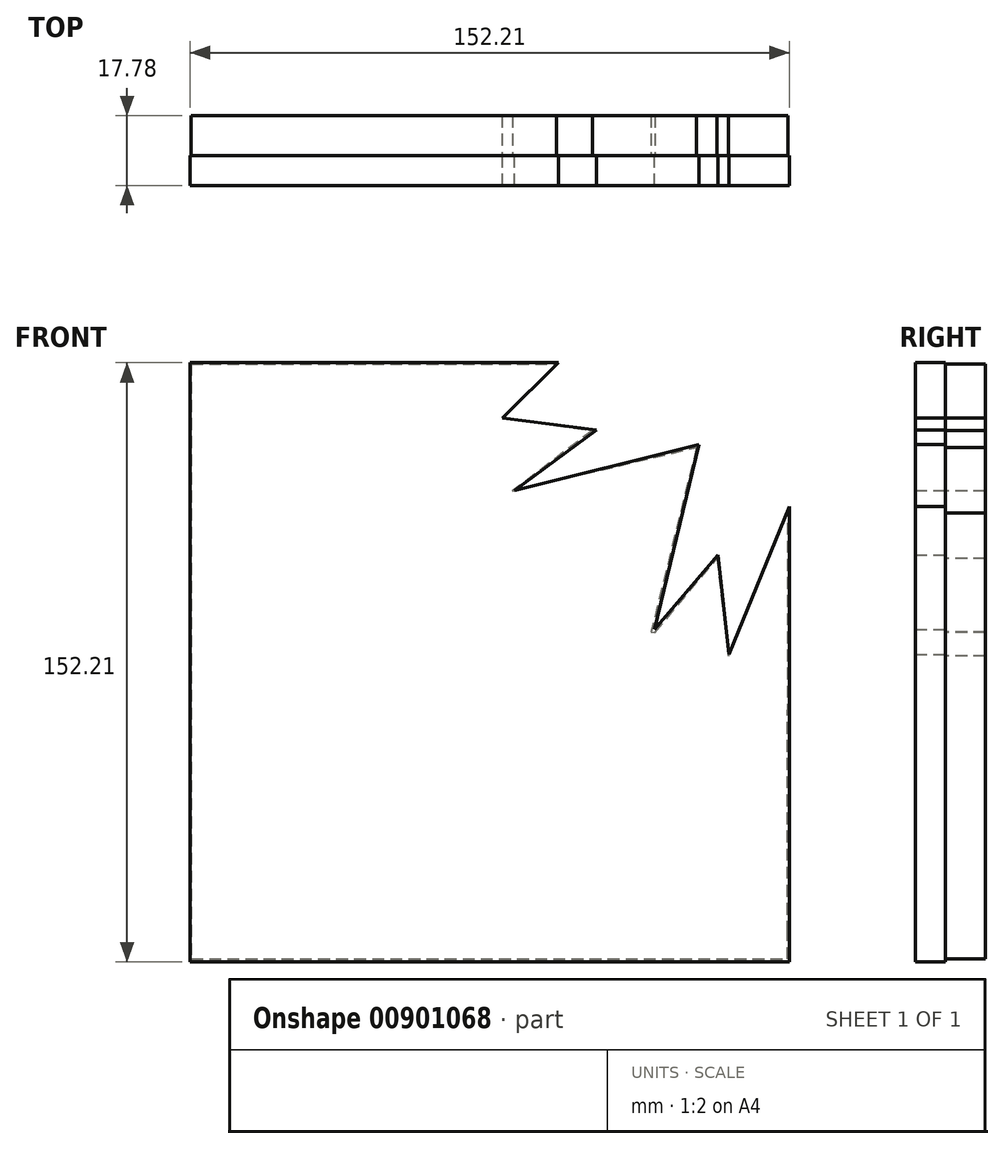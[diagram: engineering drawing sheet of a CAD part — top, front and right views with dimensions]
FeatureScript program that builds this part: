
annotation { "Feature Type Name" : "Feature", "Feature Type Description" : "" }
export const myFeature = defineFeature(function(context is Context, id is Id, definition is map)
    precondition{}
    {
        {
            var Q0;
            Q0=qCreatedBy(makeId("Front.planeOp"),FACE);
            var sketch = newSketch(context, id + "F0", { "sketchPlane" : qUnion([Q0])});
            skLineSegment(sketch, "E0.bottom", {"start": v(-76.28, 76.28) * mm, "end": v(75.93, 76.28) * mm});
            skLineSegment(sketch, "E0.top", {"start": v(-76.28, -75.93) * mm, "end": v(75.93, -75.93) * mm});
            skLineSegment(sketch, "E0.left", {"start": v(-76.28, 76.28) * mm, "end": v(-76.28, -75.93) * mm});
            skLineSegment(sketch, "E0.right", {"start": v(75.93, 76.28) * mm, "end": v(75.93, -75.93) * mm});
            skSolve(sketch);
        }
        {
            var Q0;
            Q0 = qSketchRegion(id + "F0", true);
            extrude(context, id + "F1", {"entities" : qUnion([Q0]), "depth" : 7.62 * mm, "offsetDistance" : 25.4 * mm});
        }
        {
            var Q0;
            Q0=qCreatedBy(makeId("Front.planeOp"),FACE);
            var sketch = newSketch(context, id + "F2", { "sketchPlane" : qUnion([Q0])});
            skLineSegment(sketch, "E1", {"start": v(76.04, 40.06) * mm, "end": v(60.58, 2.2) * mm});
            skLineSegment(sketch, "E2", {"start": v(60.58, 2.2) * mm, "end": v(57.8, 27.39) * mm});
            skLineSegment(sketch, "E3", {"start": v(57.8, 27.39) * mm, "end": v(41.65, 8.46) * mm});
            skLineSegment(sketch, "E4", {"start": v(41.65, 8.46) * mm, "end": v(52.94, 55.52) * mm});
            skLineSegment(sketch, "E5", {"start": v(52.94, 55.52) * mm, "end": v(6.06, 43.89) * mm});
            skLineSegment(sketch, "E6", {"start": v(6.06, 43.89) * mm, "end": v(26.9, 59.17) * mm});
            skLineSegment(sketch, "E7", {"start": v(26.9, 59.17) * mm, "end": v(3.1, 62.3) * mm});
            skLineSegment(sketch, "E8", {"start": v(3.1, 62.3) * mm, "end": v(17.34, 76.36) * mm});
            skLineSegment(sketch, "E9", {"start": v(17.34, 76.36) * mm, "end": v(76.21, 76.36) * mm});
            skLineSegment(sketch, "E10", {"start": v(76.21, 76.36) * mm, "end": v(76.04, 40.06) * mm});
            skSolve(sketch);
        }
        {
            var Q0;
            Q0 = qSketchRegion(id + "F2", true);
            extrude(context, id + "F3", {"entities" : qUnion([Q0]), "operationType" : NewBodyOperationType.REMOVE, "depth" : 7.62 * mm, "offsetDistance" : 25.4 * mm});
        }
        {
            var Q0;
            Q0=qCreatedBy(makeId("Front.planeOp"),FACE);
            var sketch = newSketch(context, id + "F4", { "sketchPlane" : qUnion([Q0])});
            skLineSegment(sketch, "E11.bottom", {"start": v(-76, 76) * mm, "end": v(-69.58, 76) * mm});
            skLineSegment(sketch, "E11.top", {"start": v(-76, -75.24) * mm, "end": v(-69.58, -75.24) * mm});
            skLineSegment(sketch, "E11.left", {"start": v(-76, 76) * mm, "end": v(-76, -75.24) * mm});
            skLineSegment(sketch, "E11.right", {"start": v(-69.58, 76) * mm, "end": v(-69.58, -75.24) * mm});
            skLineSegment(sketch, "E12.left", {"start": v(-76, -75.24) * mm, "end": v(-76, -68.64) * mm});
            skLineSegment(sketch, "E13", {"start": v(60.6, -4.53) * mm, "end": v(69.85, 12.5) * mm});
            skLineSegment(sketch, "E14", {"start": v(55.7, 20.71) * mm, "end": v(60.6, -5) * mm});
            skLineSegment(sketch, "E15", {"start": v(48.52, 50.62) * mm, "end": v(13.3, -41.64) * mm});
            skLineSegment(sketch, "E16", {"start": v(55.7, 20.71) * mm, "end": v(13.3, -41.64) * mm});
            skLineSegment(sketch, "E17", {"start": v(20.55, 57.52) * mm, "end": v(-40.88, 7.56) * mm});
            skLineSegment(sketch, "E18", {"start": v(-40.88, 7.56) * mm, "end": v(48.52, 50.62) * mm});
            skLineSegment(sketch, "E19", {"start": v(-3.6, 61.46) * mm, "end": v(20.55, 57.52) * mm});
            skLineSegment(sketch, "E20", {"start": v(17.24, 76.23) * mm, "end": v(4.4, 76.23) * mm});
            skPoint(sketch, "E21.oppositeSnap0", {"position": v(0.4, 68.85) * mm});
            skLineSegment(sketch, "E21.bottom", {"start": v(-76, 76) * mm, "end": v(9.77, 76) * mm});
            skLineSegment(sketch, "E21.left", {"start": v(-76, 76) * mm, "end": v(-76, 68.85) * mm});
            skLineSegment(sketch, "E22", {"start": v(69.85, -75.24) * mm, "end": v(69.85, 12.5) * mm});
            skLineSegment(sketch, "E23", {"start": v(-76, 68.85) * mm, "end": v(0.4, 68.85) * mm});
            skLineSegment(sketch, "E24", {"start": v(-3.6, 61.46) * mm, "end": v(0.4, 68.85) * mm});
            skLineSegment(sketch, "E25", {"start": v(-76, 76) * mm, "end": v(16.83, 76) * mm});
            skLineSegment(sketch, "E26", {"start": v(16.83, 76) * mm, "end": v(2.95, 62.27) * mm});
            skLineSegment(sketch, "E27", {"start": v(2.95, 62.27) * mm, "end": v(25.95, 59.1) * mm});
            skLineSegment(sketch, "E28", {"start": v(25.95, 59.1) * mm, "end": v(5.65, 43.7) * mm});
            skLineSegment(sketch, "E29", {"start": v(5.65, 43.7) * mm, "end": v(52.39, 54.8) * mm});
            skLineSegment(sketch, "E30", {"start": v(52.39, 54.8) * mm, "end": v(40.8, 7.84) * mm});
            skLineSegment(sketch, "E31", {"start": v(40.8, 7.84) * mm, "end": v(41.74, 7.7) * mm});
            skLineSegment(sketch, "E32", {"start": v(41.74, 7.7) * mm, "end": v(57.56, 26.6) * mm});
            skLineSegment(sketch, "E33", {"start": v(57.56, 26.6) * mm, "end": v(60.45, 1.8) * mm});
            skLineSegment(sketch, "E34", {"start": v(60.45, 1.8) * mm, "end": v(75.57, 38.13) * mm});
            skLineSegment(sketch, "E35.bottom", {"start": v(-76, -75.24) * mm, "end": v(75.46, -75.24) * mm});
            skLineSegment(sketch, "E35.top", {"start": v(-76, -68.58) * mm, "end": v(75.46, -68.58) * mm});
            skLineSegment(sketch, "E35.left", {"start": v(-76, -75.24) * mm, "end": v(-76, -68.58) * mm});
            skLineSegment(sketch, "E35.right", {"start": v(75.46, -75.24) * mm, "end": v(75.46, -68.58) * mm});
            skLineSegment(sketch, "E36", {"start": v(75.46, -68.58) * mm, "end": v(75.57, 38.13) * mm});
            skSolve(sketch);
        }
        {
            var Q0;
            Q0 = qSketchRegion(id + "F4", true);
            extrude(context, id + "F5", {"entities" : qUnion([Q0]), "operationType" : NewBodyOperationType.ADD, "oppositeDirection" : true, "depth" : 10.16 * mm, "offsetDistance" : 25.4 * mm});
        }
    });
